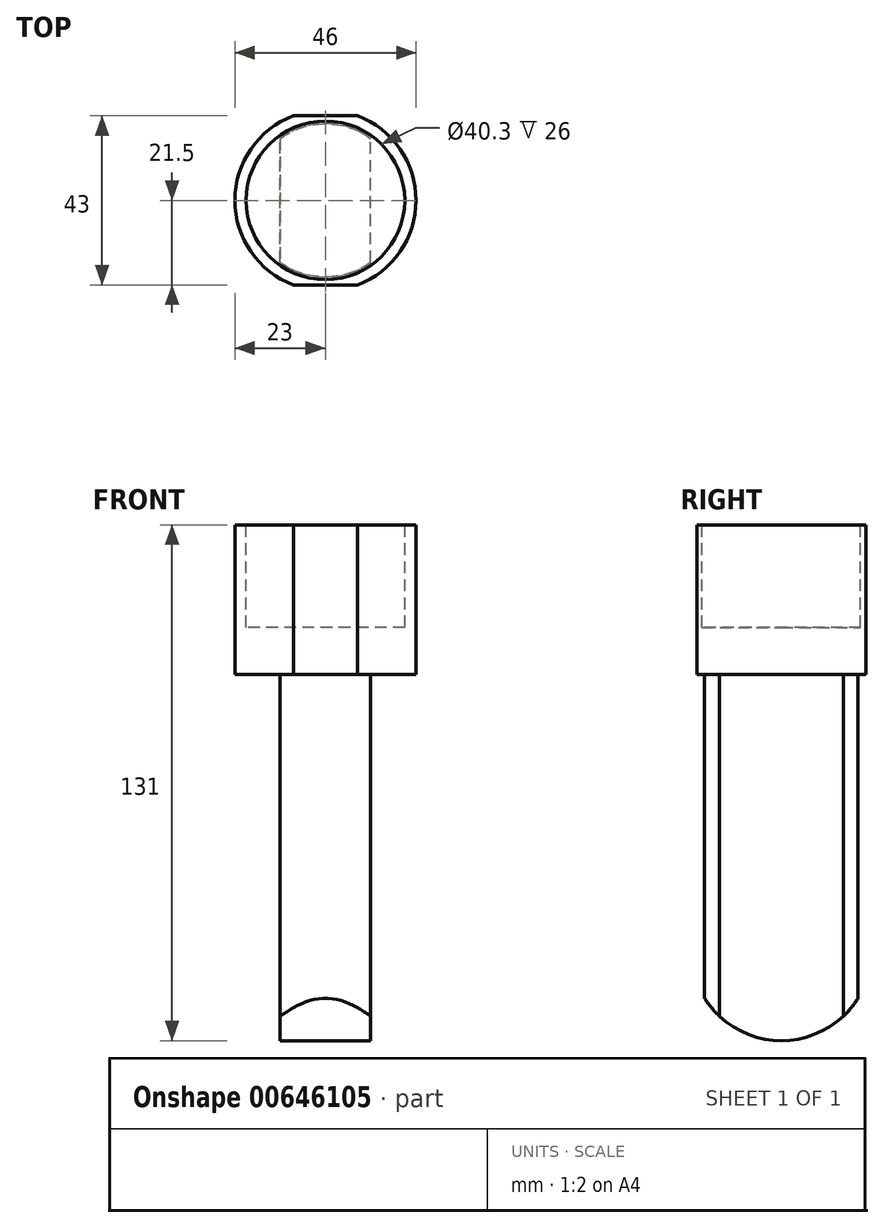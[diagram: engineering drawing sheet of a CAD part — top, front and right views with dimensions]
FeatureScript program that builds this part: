
annotation { "Feature Type Name" : "Feature", "Feature Type Description" : "" }
export const myFeature = defineFeature(function(context is Context, id is Id, definition is map)
    precondition{}
    {
        {
            var Q0;
            Q0=qCreatedBy(makeId("Top.planeOp"),FACE);
            var sketch = newSketch(context, id + "F0", { "sketchPlane" : qUnion([Q0])});
            skArc(sketch, "E0", {"start": v(-8.17, 21.5) * mm, "mid": v(-23, 0) * mm, "end": v(-8.17, -21.5) * mm});
            skLineSegment(sketch, "E1", {"start": v(-8.17, 21.5) * mm, "end": v(8.17, 21.5) * mm});
            skLineSegment(sketch, "E2.MirrorCS", {"start": v(-8.17, -21.5) * mm, "end": v(8.17, -21.5) * mm});
            skArc(sketch, "E3.trimOffspring", {"start": v(8.17, -21.5) * mm, "mid": v(23, 0) * mm, "end": v(8.17, 21.5) * mm});
            skSolve(sketch);
        }
        {
            var Q0;
            Q0=qSketchRegion(id+"F0",true);
            extrude(context, id + "F1", {"entities" : qUnion([Q0]), "depth" : 38 * mm, "offsetDistance" : 25 * mm});
        }
        {
            var Q0;
            Q0=makeQuery(id+"F1.opExtrude","CAP_FACE",FACE,{"disambiguationData":[OSD([sQuery(id+"F0.wireOp",EDGE,"E0"),sQuery(id+"F0.wireOp",EDGE,"E1"),sQuery(id+"F0.wireOp",EDGE,"E2.MirrorCS"),sQuery(id+"F0.wireOp",EDGE,"E3.trimOffspring")])],"isStart":false});
            var sketch = newSketch(context, id + "F2", { "sketchPlane" : qUnion([Q0])});
            skCircle(sketch, "E4", {"center": v(0, 0) * mm, "radius": 20.15 * mm});
            skSolve(sketch);
        }
        {
            var Q0;
            Q0=makeQuery(id+"F2.imprint","IMPRINT",FACE,{"disambiguationData":[TD([[makeQuery(id+"F2.imprint","IMPRINT",EDGE,{"derivedFrom":sQuery(id+"F2.wireOp",EDGE,"E4")}),1.0]])]});
            extrude(context, id + "F3", {"entities" : qUnion([Q0]), "operationType" : NewBodyOperationType.REMOVE, "oppositeDirection" : true, "depth" : 26 * mm, "offsetDistance" : 25 * mm});
        }
        {
            var Q0;
            Q0=makeQuery(id+"F1.opExtrude","CAP_FACE",FACE,{"disambiguationData":[OSD([sQuery(id+"F0.wireOp",EDGE,"E0"),sQuery(id+"F0.wireOp",EDGE,"E1"),sQuery(id+"F0.wireOp",EDGE,"E2.MirrorCS"),sQuery(id+"F0.wireOp",EDGE,"E3.trimOffspring")])],"isStart":true});
            var sketch = newSketch(context, id + "F4", { "sketchPlane" : qUnion([Q0])});
            skArc(sketch, "E5", {"start": v(11.5, 15.75) * mm, "mid": v(0, 19.5) * mm, "end": v(-11.5, 15.75) * mm});
            skLineSegment(sketch, "E6", {"start": v(-11.5, 15.75) * mm, "end": v(-11.5, -15.75) * mm});
            skLineSegment(sketch, "E7.MirrorCS", {"start": v(11.5, 15.75) * mm, "end": v(11.5, -15.75) * mm});
            skArc(sketch, "E8.trimOffspring", {"start": v(-11.5, -15.75) * mm, "mid": v(0, -19.5) * mm, "end": v(11.5, -15.75) * mm});
            skSolve(sketch);
        }
        {
            var Q0;
            Q0=makeQuery(id+"F4.imprint","IMPRINT",FACE,{"disambiguationData":[TD([[makeQuery(id+"F4.imprint","IMPRINT",EDGE,{"derivedFrom":sQuery(id+"F4.wireOp",EDGE,"E5")}),1.0]])]});
            extrude(context, id + "F5", {"entities" : qUnion([Q0]), "operationType" : NewBodyOperationType.ADD, "depth" : 93 * mm, "offsetDistance" : 25 * mm});
        }
        {
            var Q0;
            Q0=makeQuery(id+"F5.opExtrude","SWEPT_FACE",FACE,{"disambiguationData":[OSD([sQuery(id+"F4.wireOp",EDGE,"E6")])]});
            var sketch = newSketch(context, id + "F6", { "sketchPlane" : qUnion([Q0])});
            skArc(sketch, "E9", {"start": v(-22.67, -73.89) * mm, "mid": v(2.07, -92.9) * mm, "end": v(23, -69.77) * mm});
            skLineSegment(sketch, "E10", {"start": v(-22.67, -73.89) * mm, "end": v(-27.42, -95.71) * mm});
            skLineSegment(sketch, "E11", {"start": v(-27.42, -95.71) * mm, "end": v(39.85, -95.71) * mm});
            skLineSegment(sketch, "E12", {"start": v(39.85, -95.71) * mm, "end": v(23, -69.77) * mm});
            skSolve(sketch);
        }
        {
            var Q0;
            {var subQ0=sQuery(id+"F6.wireOp",EDGE,"E9");var subQ1=sQuery(id+"F4.wireOp",EDGE,"E6");var subQ4=makeQuery(id+"F5.opExtrude","CAP_EDGE",EDGE,{"disambiguationData":[OSD([subQ1])],"isStart":false});var subQ5=makeQuery(id+"F6.imprint","INTERSECT",VERTEX,{"derivedFrom":[subQ4,subQ0]});Q0=makeQuery(id+"F6.imprint","IMPRINT",FACE,{"disambiguationData":[TD([[makeQuery(id+"F6.imprint","IMPRINT",EDGE,{"disambiguationData":[TD([[subQ5,1.0]])],"derivedFrom":subQ0}),-1.0]])]});}
            var Q1;
            {var subQ0=sQuery(id+"F6.wireOp",EDGE,"E9");var subQ1=sQuery(id+"F4.wireOp",EDGE,"E6");var subQ4=makeQuery(id+"F5.opExtrude","CAP_EDGE",EDGE,{"disambiguationData":[OSD([subQ1])],"isStart":false});var subQ5=makeQuery(id+"F6.imprint","INTERSECT",VERTEX,{"derivedFrom":[subQ4,subQ0]});Q1=makeQuery(id+"F6.imprint","IMPRINT",FACE,{"disambiguationData":[TD([[makeQuery(id+"F6.imprint","IMPRINT",EDGE,{"disambiguationData":[TD([[subQ5,-1.0]])],"derivedFrom":subQ0}),-1.0]])]});}
            var Q2;
            {var subQ0=sQuery(id+"F6.wireOp",EDGE,"E10");Q2=makeQuery(id+"F6.imprint","IMPRINT",FACE,{"disambiguationData":[TD([[makeQuery(id+"F6.imprint","IMPRINT",EDGE,{"derivedFrom":subQ0}),1.0]])]});}
            extrude(context, id + "F7", {"entities" : qUnion([Q0, Q1, Q2]), "operationType" : NewBodyOperationType.REMOVE, "oppositeDirection" : true, "depth" : 25 * mm, "offsetDistance" : 25 * mm});
        }
    });
